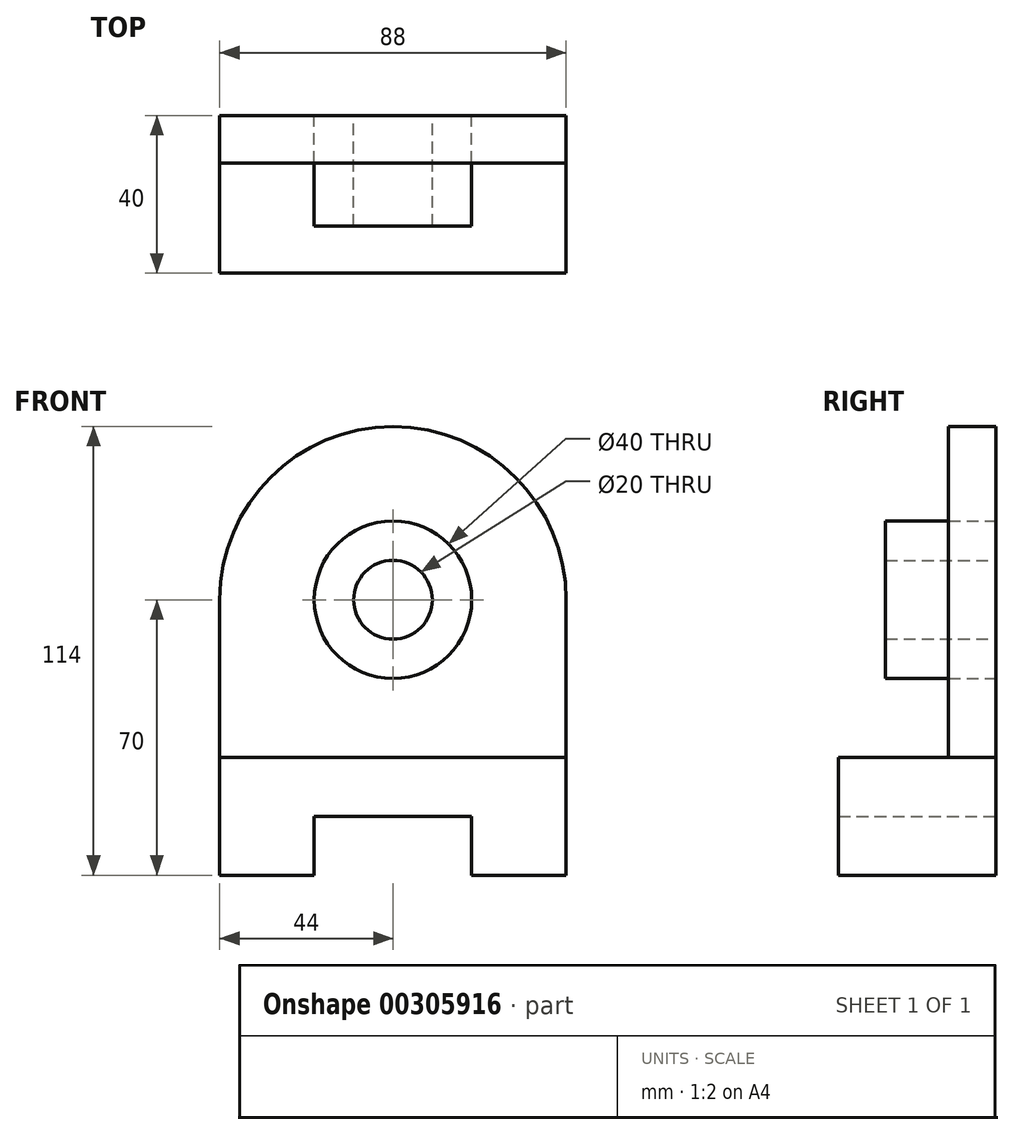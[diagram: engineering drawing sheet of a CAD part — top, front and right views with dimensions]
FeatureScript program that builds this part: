
annotation { "Feature Type Name" : "Feature", "Feature Type Description" : "" }
export const myFeature = defineFeature(function(context is Context, id is Id, definition is map)
    precondition{}
    {
        {
            var Q0;
            Q0=qCreatedBy(makeId("Front.planeOp"),FACE);
            var sketch = newSketch(context, id + "F0", { "sketchPlane" : qUnion([Q0])});
            skLineSegment(sketch, "E0", {"start": v(-44, -12) * mm, "end": v(44, -12) * mm});
            skLineSegment(sketch, "E1", {"start": v(-44, -12) * mm, "end": v(-44, -42) * mm});
            skLineSegment(sketch, "E2", {"start": v(-44, -42) * mm, "end": v(-20, -42) * mm});
            skLineSegment(sketch, "E3", {"start": v(-20, -42) * mm, "end": v(-20, -27) * mm});
            skLineSegment(sketch, "E4", {"start": v(-20, -27) * mm, "end": v(20, -27) * mm});
            skLineSegment(sketch, "E5", {"start": v(20, -27) * mm, "end": v(20, -42) * mm});
            skLineSegment(sketch, "E6", {"start": v(20, -42) * mm, "end": v(44, -42) * mm});
            skLineSegment(sketch, "E7", {"start": v(44, -42) * mm, "end": v(44, -12) * mm});
            skLineSegment(sketch, "E8", {"start": v(-44, -12) * mm, "end": v(-44, 28) * mm});
            skLineSegment(sketch, "E9", {"start": v(44, -12) * mm, "end": v(44, 28) * mm});
            skArc(sketch, "E10", {"start": v(44, 28) * mm, "mid": v(0, 72) * mm, "end": v(-44, 28) * mm});
            skCircle(sketch, "E11", {"center": v(0, 28) * mm, "radius": 20 * mm});
            skCircle(sketch, "E12", {"center": v(0, 28) * mm, "radius": 10 * mm});
            skSolve(sketch);
        }
        {
            var Q0;
            Q0=makeQuery(id+"F0.imprint","IMPRINT",FACE,{"disambiguationData":[TD([[makeQuery(id+"F0.imprint","IMPRINT",EDGE,{"derivedFrom":sQuery(id+"F0.wireOp",EDGE,"E11")}),1.0]])]});
            extrude(context, id + "F1", {"entities" : qUnion([Q0]), "depth" : 28 * mm});
        }
        {
            var Q0;
            Q0=makeQuery(id+"F0.imprint","IMPRINT",FACE,{"disambiguationData":[TD([[makeQuery(id+"F0.imprint","IMPRINT",EDGE,{"derivedFrom":sQuery(id+"F0.wireOp",EDGE,"E0")}),-1.0]])]});
            extrude(context, id + "F2", {"entities" : qUnion([Q0]), "depth" : 40 * mm});
        }
        {
            var Q0;
            Q0=makeQuery(id+"F0.imprint","IMPRINT",FACE,{"disambiguationData":[TD([[makeQuery(id+"F0.imprint","IMPRINT",EDGE,{"derivedFrom":sQuery(id+"F0.wireOp",EDGE,"E0")}),1.0]])]});
            extrude(context, id + "F3", {"entities" : qUnion([Q0]), "depth" : 12 * mm});
        }
    });
